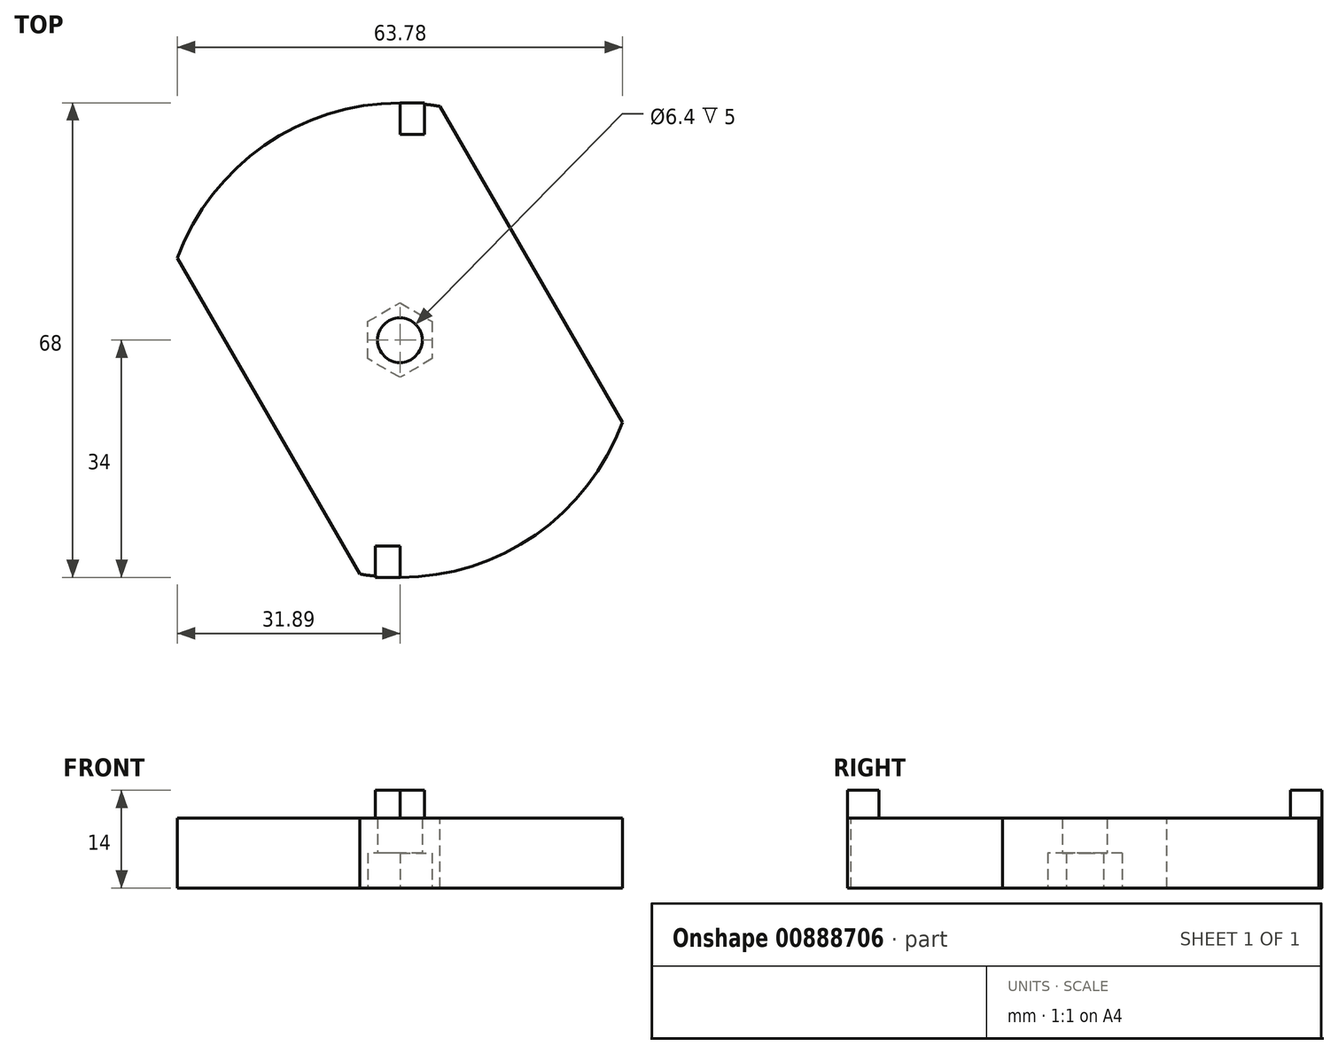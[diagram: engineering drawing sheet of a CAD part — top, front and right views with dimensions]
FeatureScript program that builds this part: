
annotation { "Feature Type Name" : "Feature", "Feature Type Description" : "" }
export const myFeature = defineFeature(function(context is Context, id is Id, definition is map)
    precondition{}
    {
        {
            var Q0;
            Q0=qCreatedBy(makeId("Top.planeOp"),FACE);
            var sketch = newSketch(context, id + "F0", { "sketchPlane" : qUnion([Q0])});
            skCircle(sketch, "E0", {"center": v(0, 0) * mm, "radius": 34 * mm});
            skCircle(sketch, "E1.cCircle", {"center": v(0, 0) * mm, "radius": 4.62 * mm, "construction": true});
            skLineSegment(sketch, "E1.0", {"start": v(4.62, 2.67) * mm, "end": v(4.62, -2.67) * mm});
            skLineSegment(sketch, "E1.1", {"start": v(4.62, -2.67) * mm, "end": v(0, -5.34) * mm});
            skLineSegment(sketch, "E1.2", {"start": v(0, -5.34) * mm, "end": v(-4.63, -2.67) * mm});
            skLineSegment(sketch, "E1.3", {"start": v(-4.62, -2.67) * mm, "end": v(-4.63, 2.67) * mm});
            skLineSegment(sketch, "E1.4", {"start": v(-4.63, 2.67) * mm, "end": v(0, 5.34) * mm});
            skLineSegment(sketch, "E1.5", {"start": v(0, 5.34) * mm, "end": v(4.62, 2.67) * mm});
            skPoint(sketch, "E1.0.midPoint", {"position": v(4.62, 0) * mm});
            skCircle(sketch, "E2", {"center": v(0, 0) * mm, "radius": 3.2 * mm});
            skSolve(sketch);
        }
        {
            var Q0;
            Q0=makeQuery(id+"F0.imprint","IMPRINT",FACE,{"disambiguationData":[TD([[makeQuery(id+"F0.imprint","IMPRINT",EDGE,{"derivedFrom":sQuery(id+"F0.wireOp",EDGE,"E0")}),1.0]])]});
            extrude(context, id + "F1", {"entities" : qUnion([Q0]), "depth" : 5 * mm, "offsetDistance" : 25 * mm});
        }
        {
            var Q0;
            Q0=makeQuery(id+"F1.opExtrude","CAP_FACE",FACE,{"disambiguationData":[OSD([sQuery(id+"F0.wireOp",EDGE,"E0"),sQuery(id+"F0.wireOp",EDGE,"E1.0"),sQuery(id+"F0.wireOp",EDGE,"E1.1"),sQuery(id+"F0.wireOp",EDGE,"E1.2"),sQuery(id+"F0.wireOp",EDGE,"E1.3"),sQuery(id+"F0.wireOp",EDGE,"E1.4"),sQuery(id+"F0.wireOp",EDGE,"E1.5")])],"isStart":false});
            var sketch = newSketch(context, id + "F2", { "sketchPlane" : qUnion([Q0])});
            skCircle(sketch, "E3", {"center": v(0, 0) * mm, "radius": 34 * mm});
            skCircle(sketch, "E4", {"center": v(0, 0) * mm, "radius": 3.2 * mm});
            skSolve(sketch);
        }
        {
            var Q0;
            Q0=makeQuery(id+"F2.imprint","IMPRINT",FACE,{"disambiguationData":[TD([[makeQuery(id+"F2.imprint","IMPRINT",EDGE,{"derivedFrom":sQuery(id+"F2.wireOp",EDGE,"E3")}),1.0]])]});
            var Q1;
            Q1=makeQuery(id+"F2.imprint","IMPRINT",FACE,{"disambiguationData":[TD([[makeQuery(id+"F2.imprint","IMPRINT",EDGE,{"derivedFrom":sQuery(id+"F2.wireOp",EDGE,"E4")}),-1.0]])]});
            extrude(context, id + "F3", {"entities" : qUnion([Q0, Q1]), "operationType" : NewBodyOperationType.ADD, "depth" : 5 * mm, "offsetDistance" : 25 * mm});
        }
        {
            var Q0;
            Q0=makeQuery(id+"F3.opExtrude","CAP_FACE",FACE,{"disambiguationData":[OSD([sQuery(id+"F2.wireOp",EDGE,"E3"),sQuery(id+"F2.wireOp",EDGE,"E4")])],"isStart":false});
            var sketch = newSketch(context, id + "F4", { "sketchPlane" : qUnion([Q0])});
            skLineSegment(sketch, "E5", {"start": v(0, 34) * mm, "end": v(0, -34) * mm, "construction": true});
            skLineSegment(sketch, "E6.bottom", {"start": v(0, 34) * mm, "end": v(3.5, 34) * mm});
            skLineSegment(sketch, "E6.top", {"start": v(0, 29.5) * mm, "end": v(3.5, 29.5) * mm});
            skLineSegment(sketch, "E6.left", {"start": v(0, 34) * mm, "end": v(0, 29.5) * mm});
            skLineSegment(sketch, "E6.right", {"start": v(3.5, 34) * mm, "end": v(3.5, 29.5) * mm});
            skLineSegment(sketch, "E7.bottom", {"start": v(0, -34) * mm, "end": v(-3.5, -34) * mm});
            skLineSegment(sketch, "E7.top", {"start": v(0, -29.5) * mm, "end": v(-3.5, -29.5) * mm});
            skLineSegment(sketch, "E7.left", {"start": v(0, -34) * mm, "end": v(0, -29.5) * mm});
            skLineSegment(sketch, "E7.right", {"start": v(-3.5, -34) * mm, "end": v(-3.5, -29.5) * mm});
            skLineSegment(sketch, "E8.bottom", {"start": v(-5.9, 53.69) * mm, "end": v(43.54, -31.96) * mm});
            skLineSegment(sketch, "E8.top", {"start": v(-43.54, 31.96) * mm, "end": v(5.9, -53.69) * mm});
            skLineSegment(sketch, "E8.left", {"start": v(-5.9, 53.69) * mm, "end": v(-43.54, 31.96) * mm});
            skLineSegment(sketch, "E8.right", {"start": v(43.54, -31.96) * mm, "end": v(5.9, -53.69) * mm});
            skPoint(sketch, "E8.middle", {"position": v(0, 0) * mm});
            skSolve(sketch);
        }
        {
            var Q0;
            {var subQ0=sQuery(id+"F4.wireOp",EDGE,"E8.bottom");var subQ1=makeQuery(id+"F3.opExtrude","CAP_EDGE",EDGE,{"disambiguationData":[OSD([sQuery(id+"F2.wireOp",EDGE,"E3")])],"isStart":false});var subQ2=makeQuery(id+"F4.imprint","INTERSECT",VERTEX,{"disambiguationData":[OD(0.0)],"derivedFrom":[subQ1,subQ0]});Q0=makeQuery(id+"F4.imprint","IMPRINT",FACE,{"disambiguationData":[TD([[makeQuery(id+"F4.imprint","IMPRINT",EDGE,{"disambiguationData":[TD([[subQ2,-1.0]])],"derivedFrom":subQ0}),1.0]])]});}
            var Q1;
            {var subQ0=sQuery(id+"F4.wireOp",EDGE,"E8.top");var subQ1=makeQuery(id+"F3.opExtrude","CAP_EDGE",EDGE,{"disambiguationData":[OSD([sQuery(id+"F2.wireOp",EDGE,"E3")])],"isStart":false});var subQ2=makeQuery(id+"F4.imprint","INTERSECT",VERTEX,{"disambiguationData":[OD(0.0)],"derivedFrom":[subQ1,subQ0]});Q1=makeQuery(id+"F4.imprint","IMPRINT",FACE,{"disambiguationData":[TD([[makeQuery(id+"F4.imprint","IMPRINT",EDGE,{"disambiguationData":[TD([[subQ2,-1.0]])],"derivedFrom":subQ0}),-1.0]])]});}
            extrude(context, id + "F5", {"entities" : qUnion([Q0, Q1]), "operationType" : NewBodyOperationType.REMOVE, "endBound" : BoundingType.THROUGH_ALL, "oppositeDirection" : true, "depth" : 25 * mm, "offsetDistance" : 25 * mm});
        }
        {
            var Q0;
            {var subQ0=sQuery(id+"F4.wireOp",EDGE,"E6.top");Q0=makeQuery(id+"F4.imprint","IMPRINT",FACE,{"disambiguationData":[TD([[makeQuery(id+"F4.imprint","IMPRINT",EDGE,{"derivedFrom":subQ0}),1.0]])]});}
            var Q1;
            {var subQ0=sQuery(id+"F4.wireOp",EDGE,"E7.top");Q1=makeQuery(id+"F4.imprint","IMPRINT",FACE,{"disambiguationData":[TD([[makeQuery(id+"F4.imprint","IMPRINT",EDGE,{"derivedFrom":subQ0}),1.0]])]});}
            extrude(context, id + "F6", {"entities" : qUnion([Q0, Q1]), "operationType" : NewBodyOperationType.ADD, "depth" : 4 * mm, "offsetDistance" : 25 * mm});
        }
    });
